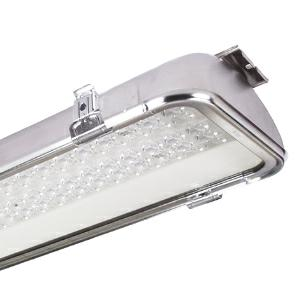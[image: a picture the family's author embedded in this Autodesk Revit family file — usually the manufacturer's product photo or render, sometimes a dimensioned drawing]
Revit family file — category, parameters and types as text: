
# Revit family: 3f_filippi_-_beta_235_93_vt_ampio_3f_filippi_-_52790_-_beta_235_led_932x50_ampio_vt_l1565
name_source: partatom
category: Lighting Fixtures
units: mm (PartAtom-declared; Revit-internal decimal feet)

## family parameters
Cut with Voids When Loaded = No
Host = Face
Light Source = No
Part Type = Normal
Room Calculation Point = No
Round Connector Dimension = Use Diameter
Shared = No

## types (1)
- 3F Filippi - Beta 235 93 VT Ampio (1 x LED, 15581 lm, 99 W, 4000 K)
    Apparent Load = 99 VA
    Approval mark = CE
    CIE Flux Codes = 55 92 99 100 100
    Color Rendering = 80
    Color Temperature = 4000 K
    Control Gear = Electronic ballast
    Default Elevation = 1800 mm
    Description = ILLUMINOTECHNICAL
Luminous efficiency 100% (DLOR 100%, ULOR 0%).
Initial luminous flux of the luminaire 15581 lm.
Wide symmetric distribution.
Installation Interdistance Transv.D = 1.18 x hu - Long.D = 1.19 x hu.
Tabular UGR (CIE 117 - 4H-8H; S=0.25H; 70/50/20): RUG 21.7 - 23.4.
Beam angle: 100° - 106°.
Luminous efficacy 157 lm/W.
Lifetime (L93/B10): 30000 h. (tq+25°C)
Lifetime (L90/B10): 50000 h. (tq+25°C)
Lifetime (L85/B10): 80000 h. (tq+25°C)
Lifetime (L80/B10): 100000 h. (tq+25°C)
Lifetime (L85/B10): 50000 h. (tq+45°C)
Sudden decreased luminous flux after 50000 hours: 0% (C0).
Photobiological safety in compliance with IEC/TR 62778: RG0 risk exempt, (IEC 62471).
In compliance with IEC/EN 62722-2-1 - IEC/EN 62717 standards.

SOURCE
2 linear LED modules 50W/840.
Energy efficiency class (UE 2019/2020 - UE 2019/2015): C.
CIE 13.3 Colour rendering index: CRI >80 (R9 <50%).
IES TM-30 Fidelity Index: Rf = 84 Rg = 95.
CCT nominal colour temperature 4000 K.
Colour initial tolerance (MacAdam): SDCM 3.

MECHANICAL
Housing in AISI 304 stainless steel, pressed in one single piece.
VT transparent glass, non-combustible, single-piece perimeter frame in stainless steel.
Oversized gear-tray reflector unit in highly reflective white painted hot-galvanised steel.
Methacrylate (PMMA) lenses with external flat surface.
Stainless steel snap-lock clips for diffuser mounting (safety n° 4 per fixture).
Luminaire with limited surface temperature. - D - (EN 60598-2-24)
Dimensions: 1565x235 mm, height 105 mm. Weight 11.345 kg.
IP65 protection degree.
Mechanical strength to impacts IK09 (10 joule).
Glow-wire test resistance 960°C.

ELECTRICAL
Halogen Free electronic wiring 230V-50/60Hz, power factor 0.95, THD <25%, constant output current, class I, 1 driver.
Power of the luminaire 99 W.
ENEC - CE.
Flicker: <4%.
Luminaire compliant with EN 60598-2-22 for power supply from a centralised emergency system CPSS (Central Power Supply System), not incorporated in the luminaire - high risk areas excluded. The default power and flux are 100% in AC and 100% in DC.
Ambient temperature from -20°C to +45°C.
Temperature class T6 max 85°C.
Quick connection via M20 3P connector with 9-13 mm tightening range.
Relative humidity UR: <85%.

INSTALLATION
Ceiling / Suspended / Wall.
All accessories dedicated to this product are available on the Catalog and on our website www.3F-Filippi.com.

APPLICATIONS
Dry, dusty indoor environments, subject to occasional water splashes.
Any environments except the ones where the luminaire materials are unsuitable.
Industrial environments, warehouses, environments where security locks are required on all clips, e.g. prisons (on request).
Environments in which it is necessary a total protection against falling fragments (eg environments with foodstuffs or machines with moving parts or with extreme temperature changes), use luminaires with laminated glass.
Tempered glass is not immune to falling fragments from harmless and caused by shocks or exceptionally derived from the tempering process.

WARNING
Fixture not suitable for cold stores with an ambient temperature <0°C and/or relative humidity >85%.
Luminaire designed for disposal/recycling at end-of-life.
Replaceable (LED only) light source by a professional. Replaceable control gear by a professional.
    Height = 105 mm
    Lamp = 1 x LED
    Lamp Light Flux = 15581 lm
    Lamp Power = 99 W
    Lamp count = 1
    Length = 1565 mm
    Lifetime = 50000 h
    Luminous efficacy = 157 lm/W
    Manufacturer = 3F Filippi
    ModVariant = No
    Model = 3F Filippi - 52790 - Beta 235 LED 932x50 AMPIO VT L1565
    Mounting Place = Ceiling
    Mounting Type = Pendant
    Number of Poles = 1
    OnlyDefault = Yes
    Power Factor = 1
    Product Name = 3F Filippi - Beta 235 93 VT Ampio
    Product group = pendant luminaire
    ProductGroupID = 9
    Protection Class = Protection class I
    Protection Degree = IP 65
    RLX_Detail_Level = 1
    RLX_Emergency_Light_Flux = 0 lm
    RLX_Emergency_Type = 0
    RLX_Emergency_Type_DB = No
    RlxData = <blob elided: 89357 chars, md5=5c61da38>
    Socket = socket
    Standby Power = 0 W
    System Light Flux = 15581 lm
    System Power = 99 W
    Type Comments = Product without accessories
    Type Image = 3ffilippi_52790.jpg
    URL = http://relux.com
    VarID = ---
    Voltage = 0 V
    Weight = 0.00 kg
    Width = 235 mm

## geometry (parser evidence)
native form markers: Blend x4, Sweep x12
no freeform markers — native parametric forms only
